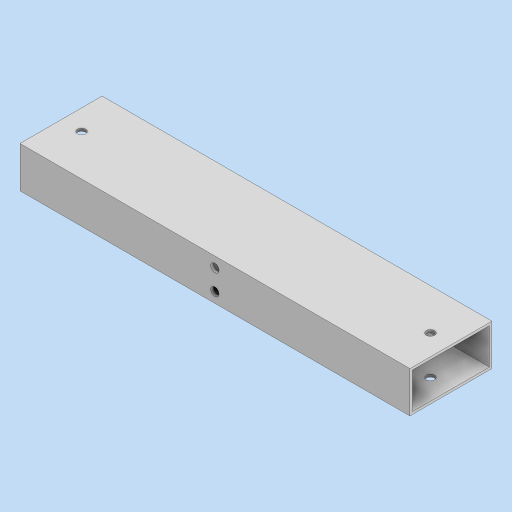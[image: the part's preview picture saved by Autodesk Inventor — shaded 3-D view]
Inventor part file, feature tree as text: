
AUTODESK INVENTOR PART (.ipt)
format: ipt  version: 2024 (Build 280153000, 153)  size: 126,464 bytes
history: native  units: in
note: dims shown in document units (in); Inventor stores cm internally (conversion verified against a paired STEP export)
features: extrude x3, sketch x3, projected_geometry x2
ambient origin geometry x8: Origin, YZ Plane, XZ Plane, XY Plane, X Axis, Y Axis, Z Axis, Center Point
bodies: Solid1 (feature_tree)
feature tree (8):
  extrude  "Extrusion1"  Depth=2.0in
  extrude  "Extrusion2"  Depth=9.5in TaperAngle=0.0deg
  extrude  "Extrusion3"  Depth=9.5in
  sketch  "Sketch1"  dims[d0=1.0in d1=2.0in]
  sketch  "Sketch2"  dims[d2=0.0625in d3=9.5in d4=0.0in]
  projected_geometry  "Projected Loop1"
  sketch  "Sketch3"  dims[d5=0.203in d6=0.5in d7=0.203in d8=0.5in d9=1.0in d10=1.0in d11=1.0in d12=0.0in d13=0.203in d14=0.203in d15=4.75in d16=4.75in d17=0.25in d18=0.25in d19=9.5in d20=0.0in]
  projected_geometry  "Projected Loop2"
